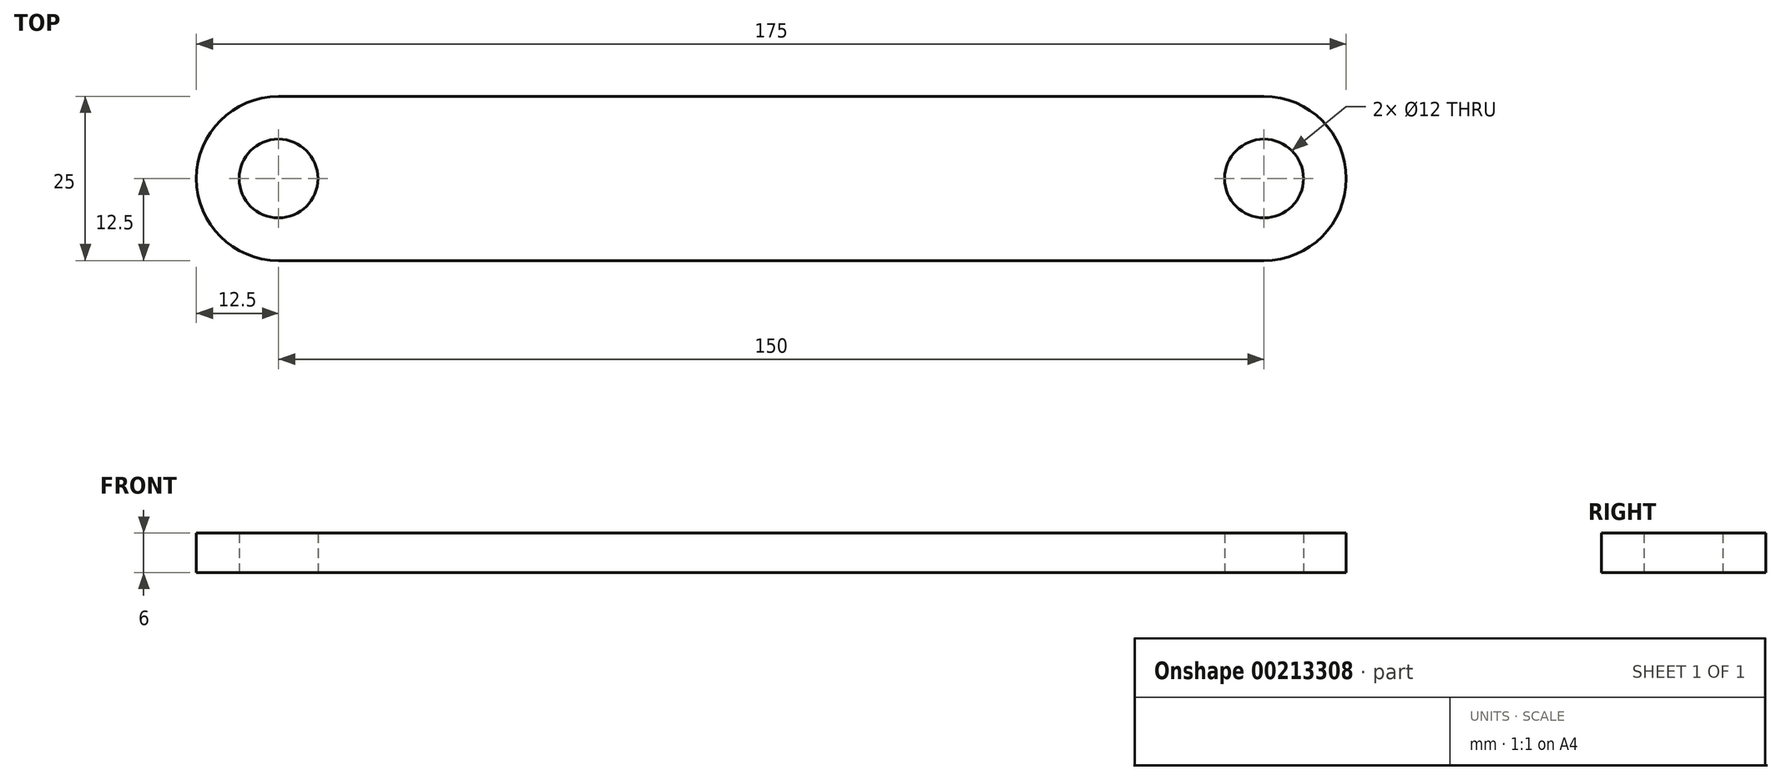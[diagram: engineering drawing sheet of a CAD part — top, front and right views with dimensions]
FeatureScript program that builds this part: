
annotation { "Feature Type Name" : "Feature", "Feature Type Description" : "" }
export const myFeature = defineFeature(function(context is Context, id is Id, definition is map)
    precondition{}
    {
        {
            var Q0;
            Q0=qCreatedBy(makeId("Top.planeOp"),FACE);
            var sketch = newSketch(context, id + "F0", { "sketchPlane" : qUnion([Q0])});
            skCircle(sketch, "E0", {"center": v(-75, 0) * mm, "radius": 6 * mm});
            skCircle(sketch, "E1", {"center": v(75, 0) * mm, "radius": 6 * mm});
            skArc(sketch, "E2", {"start": v(-75, 12.5) * mm, "mid": v(-87.5, 0) * mm, "end": v(-75, -12.5) * mm});
            skArc(sketch, "E3", {"start": v(75, -12.5) * mm, "mid": v(87.5, 0) * mm, "end": v(75, 12.5) * mm});
            skLineSegment(sketch, "E4", {"start": v(-75, -12.5) * mm, "end": v(75, -12.5) * mm});
            skLineSegment(sketch, "E5", {"start": v(75, 12.5) * mm, "end": v(-75, 12.5) * mm});
            skSolve(sketch);
        }
        {
            var Q0;
            Q0=makeQuery(id+"F0.imprint","IMPRINT",FACE,{"disambiguationData":[TD([[makeQuery(id+"F0.imprint","IMPRINT",EDGE,{"derivedFrom":sQuery(id+"F0.wireOp",EDGE,"E0")}),-1.0]])]});
            extrude(context, id + "F1", {"entities" : qUnion([Q0]), "depth" : 6 * mm});
        }
    });
